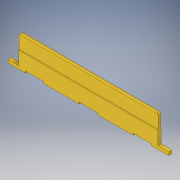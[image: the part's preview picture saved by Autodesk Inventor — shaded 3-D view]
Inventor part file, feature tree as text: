
AUTODESK INVENTOR PART (.ipt)
format: ipt  version: 2019 (Build 230136000, 136)  size: 156,160 bytes
history: native  units: in
note: dims shown in document units (in); Inventor stores cm internally (conversion verified against a paired STEP export)
features: other x7, extrude x2, sketch x2
ambient origin geometry x8: Origin, YZ Plane, XZ Plane, XY Plane, X Axis, Y Axis, Z Axis, Center Point
bodies: Solid1 (feature_tree)
feature tree (11):
  extrude  "Extrusion1"  Depth=0.7874in TaperAngle=0.0deg
  extrude  "Extrusion2"  [1 undecoded]
  other  "integral_metal_plane_XY"
  other  "integral_metal_plane_YZ"
  other  "integral_metal_plane_ZX"
  other  "integral_metal_plane_X"
  other  "integral_metal_plane_Y"
  other  "integral_metal_plane_Z"
  other  "integral_metal_plane_Center"
  sketch  "Sketch_1"  dims[d0=0.0315in d1=0.0in d2=0.7874in d3=0.0in]
  sketch  "Sketch_2"
note: 1 required parameter value undecoded (feature->parameter linkage not recoverable at this tier; creation-order binding heuristic only, values carry confidence <= 0.55)
